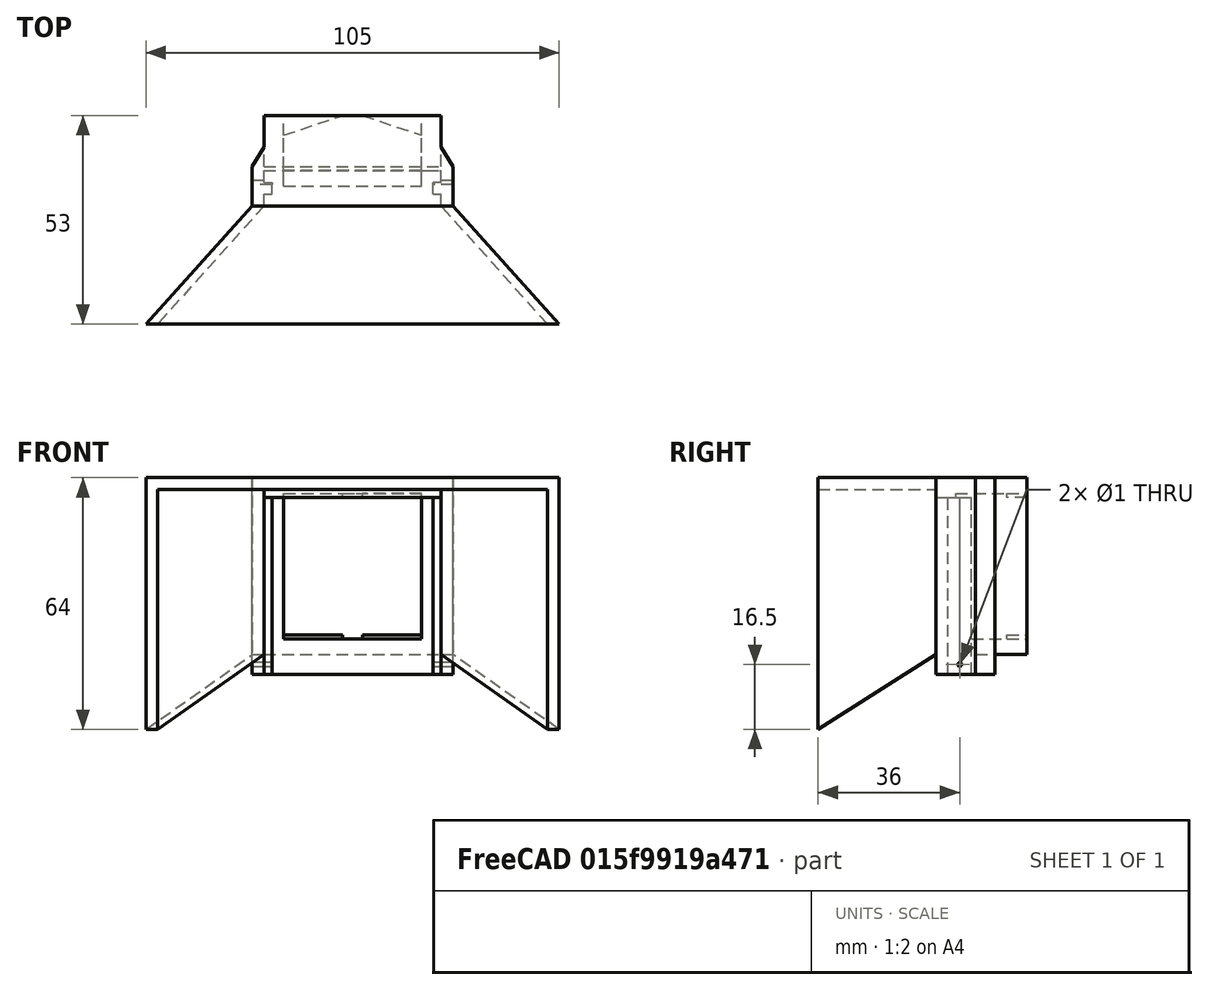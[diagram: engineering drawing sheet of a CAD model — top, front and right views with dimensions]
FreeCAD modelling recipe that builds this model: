
FCSTD DOCUMENT  (FreeCAD 0.20R29603 (Git))
Label: Spritzschutz
License: All rights reserved
LicenseURL: http://en.wikipedia.org/wiki/All_rights_reserved
objects: TechDraw::DrawViewDimension×27, TechDraw::DrawProjGroupItem×15, PartDesign::AdditiveBox×5, PartDesign::SubtractiveBox×4, PartDesign::AdditiveWedge×3, TechDraw::DrawSVGTemplate×2, PartDesign::Body×2, PartDesign::SubtractiveWedge×2, TechDraw::DrawPage×2, TechDraw::DrawProjGroup×2, App::MeasureDistance×1, PartDesign::SubtractiveCylinder×1, TechDraw::DrawViewSection×1
note: 32 computed .brp shape members not serialized (recipe doc carries the construction recipe); baked Part::Feature solids carry a one-line shape summary decoded from their .brp

FEATURE [App::MeasureDistance] Distance  label="Distance: 0,87 mm"
  Distance = 0.87465
  P1 = (0,7.01825,-5)
  P2 = (-0.871183,7.09606,-5)
FEATURE [TechDraw::DrawSVGTemplate] Template
  EditableTexts = Designed_by_Name=B. Schulze; Drawing_number=1; FC-Date=13.09.2023; FC-SC=1:2; FC-SH=8; FC-Title=Eisdosierer; Subtitle=Spritzschutz Teil 1
  Height = 210
  Orientation = 1
  Width = 297
FEATURE [TechDraw::DrawSVGTemplate] Template001
  EditableTexts = Designed_by_Name=B. Schulze; Drawing_number=1; FC-Date=13.09.2023; FC-SC=1:2; FC-SH=9; FC-Title=Eisdosierer; Subtitle=Spritzschutz Teil2
  Height = 210
  Orientation = 1
  Width = 297
FEATURE [PartDesign::Body] Body  label="Teil1"
  Group = -> [Box,Wedge,Box001,Box002,Wedge004,Wedge005,Box005,Box006,Box007,Box008,Box009,Cylinder,Box010]
  Origin = -> Origin
  Tip = -> Box010
FEATURE [PartDesign::AdditiveBox] Box
  AttacherType = Attacher::AttachEngine3D
  Height = 45
  Length = 45
  MapMode = 2
  Support = -> [Body]
  Width = 20
FEATURE [PartDesign::SubtractiveWedge] Wedge
  AttacherType = Attacher::AttachEngine3D
  AttachmentOffset = pos=(5,15,4) rot=(0,0,1;0rad)
  BaseFeature = -> Box
  MapMode = 2
  Placement = pos=(5,15,4) rot=(0,0,1;0rad)
  Support = -> [Body]
  X2max = 20
  X2min = 15
  Xmax = 35
  Xmin = 0
  Ymax = 5
  Ymin = 0
  Z2max = 37
  Z2min = 0
  Zmax = 37
  Zmin = 0
FEATURE [PartDesign::SubtractiveBox] Box001
  AttacherType = Attacher::AttachEngine3D
  AttachmentOffset = pos=(5,0,5) rot=(0,0,1;0rad)
  BaseFeature = -> Wedge
  Height = 35
  Length = 35
  MapMode = 2
  Placement = pos=(5,0,5) rot=(0,0,1;0rad)
  Support = -> [Body]
  Width = 21
FEATURE [PartDesign::SubtractiveBox] Box002
  AttacherType = Attacher::AttachEngine3D
  AttachmentOffset = pos=(5,0,4) rot=(0,0,1;0rad)
  BaseFeature = -> Box001
  Height = 37
  Length = 35
  MapMode = 2
  Placement = pos=(5,0,4) rot=(0,0,1;0rad)
  Support = -> [Body]
  Width = 15
FEATURE [PartDesign::Body] Body002  label="Teil2"
  Group = -> [Wedge002,Wedge003]
  Origin = -> Origin002
  Placement = pos=(0,-3,0) rot=(0,0,1;0rad)
  Tip = -> Wedge003
FEATURE [PartDesign::AdditiveWedge] Wedge002
  AttacherType = Attacher::AttachEngine3D
  AttachmentOffset = pos=(-30,-30,45) rot=(0,1,0;1.5708rad)
  MapMode = 2
  Placement = pos=(-30,-30,45) rot=(0,1,0;1.5708rad)
  Support = -> [Body]
  X2max = 45
  X2min = 0
  Xmax = 64
  Xmin = 0
  Ymax = 30
  Ymin = 0
  Z2max = 78
  Z2min = 27
  Zmax = 105
  Zmin = 0
FEATURE [PartDesign::SubtractiveWedge] Wedge003
  AttacherType = Attacher::AttachEngine3D
  AttachmentOffset = pos=(-27,-30,42) rot=(0,1,0;1.5708rad)
  BaseFeature = -> Wedge002
  MapMode = 2
  Placement = pos=(-27,-30,42) rot=(0,1,0;1.5708rad)
  Support = -> [Body]
  X2max = 45
  X2min = 0
  Xmax = 61
  Xmin = 0
  Ymax = 30
  Ymin = 0
  Z2max = 72
  Z2min = 27
  Zmax = 99
  Zmin = 0
FEATURE [PartDesign::AdditiveWedge] Wedge004
  AttacherType = Attacher::AttachEngine3D
  AttachmentOffset = pos=(-3,7,-5) rot=(0,0,1;0rad)
  BaseFeature = -> Box002
  MapMode = 2
  Placement = pos=(-3,7,-5) rot=(0,0,1;0rad)
  Support = -> [Body]
  X2max = 3
  X2min = 3
  Xmax = 3
  Xmin = 0
  Ymax = 5
  Ymin = 0
  Z2max = 50
  Z2min = 0
  Zmax = 50
  Zmin = 0
FEATURE [PartDesign::AdditiveWedge] Wedge005
  AttacherType = Attacher::AttachEngine3D
  AttachmentOffset = pos=(45,7,-5) rot=(0,0,1;0rad)
  BaseFeature = -> Wedge004
  MapMode = 2
  Placement = pos=(45,7,-5) rot=(0,0,1;0rad)
  Support = -> [Body]
  X2max = 0
  X2min = 0
  Xmax = 3
  Xmin = 0
  Ymax = 5
  Ymin = 0
  Z2max = 50
  Z2min = 0
  Zmax = 50
  Zmin = 0
FEATURE [PartDesign::AdditiveBox] Box005
  AttacherType = Attacher::AttachEngine3D
  AttachmentOffset = pos=(0,0,-5) rot=(0,0,1;0rad)
  BaseFeature = -> Wedge005
  Height = 5
  Length = 45
  MapMode = 2
  Placement = pos=(0,0,-5) rot=(0,0,1;0rad)
  Support = -> [Body]
  Width = 7
FEATURE [PartDesign::SubtractiveBox] Box006
  AttacherType = Attacher::AttachEngine3D
  AttachmentOffset = pos=(0,3,-5) rot=(0,0,1;0rad)
  BaseFeature = -> Box005
  Height = 45
  Length = 45
  MapMode = 2
  Placement = pos=(0,3,-5) rot=(0,0,1;0rad)
  Support = -> [Body]
  Width = 3
FEATURE [PartDesign::AdditiveBox] Box007
  AttacherType = Attacher::AttachEngine3D
  AttachmentOffset = pos=(-3,-3,-5) rot=(0,0,1;0rad)
  BaseFeature = -> Box006
  Height = 50
  Length = 3
  MapMode = 2
  Placement = pos=(-3,-3,-5) rot=(0,0,1;0rad)
  Support = -> [Body]
  Width = 10
FEATURE [PartDesign::AdditiveBox] Box008
  AttacherType = Attacher::AttachEngine3D
  AttachmentOffset = pos=(45,-3,-5) rot=(0,0,1;0rad)
  BaseFeature = -> Box007
  Height = 50
  Length = 3
  MapMode = 2
  Placement = pos=(45,-3,-5) rot=(0,0,1;0rad)
  Support = -> [Body]
  Width = 10
FEATURE [PartDesign::SubtractiveBox] Box009
  AttacherType = Attacher::AttachEngine3D
  AttachmentOffset = pos=(2,0,-5) rot=(0,0,1;0rad)
  BaseFeature = -> Box008
  Height = 45
  Length = 41
  MapMode = 2
  Placement = pos=(2,0,-5) rot=(0,0,1;0rad)
  Support = -> [Body]
  Width = 3
FEATURE [PartDesign::SubtractiveCylinder] Cylinder
  Angle = 360
  AttacherType = Attacher::AttachEngine3D
  AttachmentOffset = pos=(-3,3,-2.5) rot=(0,1,0;1.5708rad)
  BaseFeature = -> Box009
  FirstAngle = 0
  Height = 51
  MapMode = 2
  Placement = pos=(-3,3,-2.5) rot=(0,1,0;1.5708rad)
  Radius = 0.5
  SecondAngle = 0
  Support = -> [Body]
FEATURE [PartDesign::AdditiveBox] Box010
  AttacherType = Attacher::AttachEngine3D
  AttachmentOffset = pos=(0,-3,40) rot=(0,0,1;0rad)
  BaseFeature = -> Cylinder
  Height = 5
  Length = 45
  MapMode = 2
  Placement = pos=(0,-3,40) rot=(0,0,1;0rad)
  Support = -> [Body]
  Width = 5
FEATURE [TechDraw::DrawPage] Page
  KeepUpdated = true
  NextBalloonIndex = 1
  ProjectionType = 0
  Template = -> Template
  Views = -> [ProjGroup,Dimension,Dimension001,Dimension002,Dimension003,Dimension004,Dimension005,Dimension006,Dimension007,SectionView,Dimension008,Dimension009,Dimension010,Dimension011,Dimension012,Dimension013,Dimension014]
FEATURE [TechDraw::DrawProjGroup] ProjGroup
  Anchor = -> ProjItem
  AutoDistribute = false
  LockPosition = false
  ProjectionType = 0
  Rotation = 0
  Scale = 0.5
  ScaleType = 2
  Source = -> [Body]
  Views = -> [ProjItem,ProjItem001,ProjItem002,ProjItem003,ProjItem004,ProjItem005,ProjItem007,ProjItem008]
  X = 102.37
  Y = 112.924
  spacingX = 15
  spacingY = 15
FEATURE [TechDraw::DrawProjGroupItem] ProjItem  label="Front"
  CoarseView = false
  Direction = (0,0,-1)
  Focus = 100
  HardHidden = false
  IsoCount = 0
  IsoHidden = false
  IsoVisible = false
  LockPosition = true
  Perspective = false
  Rotation = 0
  RotationVector = (1,0,0)
  Scale = 0.5
  ScaleType = 2
  SeamHidden = false
  SeamVisible = true
  SmoothHidden = false
  SmoothVisible = true
  Source = -> [Body]
  Type = 0
  X = 0
  XDirection = (1,0,0)
  Y = 0
FEATURE [TechDraw::DrawProjGroupItem] ProjItem001  label="FrontBottomRight"
  CoarseView = false
  Direction = (0.57735,0.57735,-0.57735)
  Focus = 100
  HardHidden = false
  IsoCount = 0
  IsoHidden = false
  IsoVisible = false
  LockPosition = false
  Perspective = false
  Rotation = 0
  RotationVector = (1,0,0)
  Scale = 0.5
  ScaleType = 2
  SeamHidden = false
  SeamVisible = true
  SmoothHidden = false
  SmoothVisible = true
  Source = -> [Body]
  Type = 9
  X = -50.7089
  XDirection = (0.707107,0,0.707107)
  Y = 50.7089
FEATURE [TechDraw::DrawProjGroupItem] ProjItem002  label="Bottom"
  CoarseView = false
  Direction = (0,1,0)
  Focus = 100
  HardHidden = false
  IsoCount = 0
  IsoHidden = false
  IsoVisible = false
  LockPosition = false
  Perspective = false
  Rotation = 0
  RotationVector = (1,0,0)
  Scale = 0.5
  ScaleType = 2
  SeamHidden = false
  SeamVisible = true
  SmoothHidden = false
  SmoothVisible = true
  Source = -> [Body]
  Type = 5
  X = 0
  XDirection = (1,0,0)
  Y = 50.7089
FEATURE [TechDraw::DrawProjGroupItem] ProjItem003  label="FrontBottomLeft"
  CoarseView = false
  Direction = (-0.57735,0.57735,-0.57735)
  Focus = 100
  HardHidden = false
  IsoCount = 0
  IsoHidden = false
  IsoVisible = false
  LockPosition = false
  Perspective = false
  Rotation = 0
  RotationVector = (1,0,0)
  Scale = 0.5
  ScaleType = 2
  SeamHidden = false
  SeamVisible = true
  SmoothHidden = false
  SmoothVisible = true
  Source = -> [Body]
  Type = 8
  X = 127.121
  XDirection = (0.707107,0,-0.707107)
  Y = 53.4258
FEATURE [TechDraw::DrawProjGroupItem] ProjItem004  label="Left"
  CoarseView = false
  Direction = (-1,0,-1e-16)
  Focus = 100
  HardHidden = false
  IsoCount = 0
  IsoHidden = false
  IsoVisible = false
  LockPosition = false
  Perspective = false
  Rotation = 0
  RotationVector = (1,0,0)
  Scale = 0.5
  ScaleType = 2
  SeamHidden = false
  SeamVisible = true
  SmoothHidden = false
  SmoothVisible = true
  Source = -> [Body]
  Type = 1
  X = 50.7089
  XDirection = (1e-16,0,-1)
  Y = 0
FEATURE [TechDraw::DrawProjGroupItem] ProjItem005  label="Rear"
  CoarseView = false
  Direction = (0,0,1)
  Focus = 100
  HardHidden = false
  IsoCount = 0
  IsoHidden = false
  IsoVisible = false
  LockPosition = false
  Perspective = false
  Rotation = 0
  RotationVector = (1,0,0)
  Scale = 0.5
  ScaleType = 2
  SeamHidden = false
  SeamVisible = true
  SmoothHidden = false
  SmoothVisible = true
  Source = -> [Body]
  Type = 3
  X = 101.418
  XDirection = (-1,0,0)
  Y = 0
FEATURE [TechDraw::DrawProjGroupItem] ProjItem007  label="Top"
  CoarseView = false
  Direction = (0,-1,0)
  Focus = 100
  HardHidden = false
  IsoCount = 0
  IsoHidden = false
  IsoVisible = false
  LockPosition = false
  Perspective = false
  Rotation = 0
  RotationVector = (1,0,0)
  Scale = 0.5
  ScaleType = 2
  SeamHidden = false
  SeamVisible = true
  SmoothHidden = false
  SmoothVisible = true
  Source = -> [Body]
  Type = 4
  X = 0
  XDirection = (1,0,0)
  Y = -50.7089
FEATURE [TechDraw::DrawProjGroupItem] ProjItem008  label="FrontTopRight"
  CoarseView = false
  Direction = (0.57735,-0.57735,-0.57735)
  Focus = 100
  HardHidden = false
  IsoCount = 0
  IsoHidden = false
  IsoVisible = false
  LockPosition = false
  Perspective = false
  Rotation = 0
  RotationVector = (1,0,0)
  Scale = 0.5
  ScaleType = 2
  SeamHidden = false
  SeamVisible = true
  SmoothHidden = false
  SmoothVisible = true
  Source = -> [Body]
  Type = 7
  X = -60.5262
  XDirection = (0.707107,0,0.707107)
  Y = -23.5822
FEATURE [TechDraw::DrawViewDimension] Dimension
  AngleOverride = false
  Arbitrary = false
  ArbitraryTolerances = false
  EqualTolerance = true
  ExtensionAngle = 0
  FormatSpec = %.2w
  FormatSpecOverTolerance = %+.2w
  FormatSpecUnderTolerance = %+.2w
  Inverted = false
  LineAngle = 0
  LockPosition = false
  MeasureType = 1
  OverTolerance = 0
  References2D = -> [ProjItem004]
  Rotation = 0
  ScaleType = 0
  TheoreticalExact = false
  Type = 1
  UnderTolerance = 0
  X = -1.15522
  Y = -6.8516
FEATURE [TechDraw::DrawViewDimension] Dimension001
  AngleOverride = false
  Arbitrary = false
  ArbitraryTolerances = false
  EqualTolerance = true
  ExtensionAngle = 0
  FormatSpec = %.2w
  FormatSpecOverTolerance = %+.2w
  FormatSpecUnderTolerance = %+.2w
  Inverted = false
  LineAngle = 0
  LockPosition = false
  MeasureType = 1
  OverTolerance = 0
  References2D = -> [ProjItem004]
  Rotation = 0
  ScaleType = 0
  TheoreticalExact = false
  Type = 1
  UnderTolerance = 0
  X = 0.758231
  Y = 19.4339
FEATURE [TechDraw::DrawViewDimension] Dimension002
  AngleOverride = false
  Arbitrary = false
  ArbitraryTolerances = false
  EqualTolerance = true
  ExtensionAngle = 0
  FormatSpec = %.2w
  FormatSpecOverTolerance = %+.2w
  FormatSpecUnderTolerance = %+.2w
  Inverted = false
  LineAngle = 0
  LockPosition = false
  MeasureType = 1
  OverTolerance = 0
  References2D = -> [ProjItem005]
  Rotation = 0
  ScaleType = 0
  TheoreticalExact = false
  Type = 1
  UnderTolerance = 0
  X = 0
  Y = -13.5604
FEATURE [TechDraw::DrawViewDimension] Dimension003
  AngleOverride = false
  Arbitrary = false
  ArbitraryTolerances = false
  EqualTolerance = true
  ExtensionAngle = 0
  FormatSpec = %.2w
  FormatSpecOverTolerance = %+.2w
  FormatSpecUnderTolerance = %+.2w
  Inverted = false
  LineAngle = 0
  LockPosition = false
  MeasureType = 1
  OverTolerance = 0
  References2D = -> [ProjItem005]
  Rotation = 0
  ScaleType = 0
  TheoreticalExact = false
  Type = 2
  UnderTolerance = 0
  X = -24.9622
  Y = -0.098174
FEATURE [TechDraw::DrawViewDimension] Dimension004
  AngleOverride = false
  Arbitrary = false
  ArbitraryTolerances = false
  EqualTolerance = true
  ExtensionAngle = 0
  FormatSpec = %.2w
  FormatSpecOverTolerance = %+.2w
  FormatSpecUnderTolerance = %+.2w
  Inverted = false
  LineAngle = 0
  LockPosition = false
  MeasureType = 1
  OverTolerance = 0
  References2D = -> [ProjItem005]
  Rotation = 0
  ScaleType = 0
  TheoreticalExact = false
  Type = 2
  UnderTolerance = 0
  X = -18.8757
  Y = 6.06147
FEATURE [TechDraw::DrawViewDimension] Dimension005
  AngleOverride = false
  Arbitrary = false
  ArbitraryTolerances = false
  EqualTolerance = true
  ExtensionAngle = 0
  FormatSpec = %.2w
  FormatSpecOverTolerance = %+.2w
  FormatSpecUnderTolerance = %+.2w
  Inverted = false
  LineAngle = 0
  LockPosition = false
  MeasureType = 1
  OverTolerance = 0
  References2D = -> [ProjItem005]
  Rotation = 0
  ScaleType = 0
  TheoreticalExact = false
  Type = 2
  UnderTolerance = 0
  X = 27.4294
  Y = -1.02823
FEATURE [TechDraw::DrawViewDimension] Dimension006
  AngleOverride = false
  Arbitrary = false
  ArbitraryTolerances = false
  EqualTolerance = true
  ExtensionAngle = 0
  FormatSpec = %.2w
  FormatSpecOverTolerance = %+.2w
  FormatSpecUnderTolerance = %+.2w
  Inverted = false
  LineAngle = 0
  LockPosition = false
  MeasureType = 1
  OverTolerance = 0
  References2D = -> [ProjItem005]
  Rotation = 0
  ScaleType = 0
  TheoreticalExact = false
  Type = 0
  UnderTolerance = 0
  X = 16.153
  Y = -6.82513
FEATURE [TechDraw::DrawViewDimension] Dimension007
  AngleOverride = false
  Arbitrary = false
  ArbitraryTolerances = false
  EqualTolerance = true
  ExtensionAngle = 0
  FormatSpec = %.2w
  FormatSpecOverTolerance = %+.2w
  FormatSpecUnderTolerance = %+.2w
  Inverted = false
  LineAngle = 0
  LockPosition = false
  MeasureType = 1
  OverTolerance = 0
  References2D = -> [ProjItem005]
  Rotation = 0
  ScaleType = 0
  TheoreticalExact = false
  Type = 1
  UnderTolerance = 0
  X = 12.2194
  Y = 12.5831
FEATURE [TechDraw::DrawViewSection] SectionView  label="Section  - "
  BaseView = -> ProjItem002
  CoarseView = false
  CutSurfaceDisplay = 2
  Direction = (0,0,1)
  FileGeomPattern = <path> 0.20/data/Mod/TechDraw/PAT/FCPAT.pat
  FileHatchPattern = <path> 0.20/data/Mod/TechDraw/Patterns/simple.svg
  Focus = 100
  FuseBeforeCut = false
  HardHidden = false
  HatchScale = 1
  IsoCount = 0
  IsoHidden = false
  IsoVisible = false
  LockPosition = false
  NameGeomPattern = Diamant
  Perspective = false
  Rotation = 0
  ScaleType = 2
  SeamHidden = false
  SeamVisible = true
  SectionDirection = 2
  SectionNormal = (0,0,1)
  SectionOrigin = (22.5,7.5,39)
  SmoothHidden = false
  SmoothVisible = true
  Source = -> [Body]
  X = 158.364
  XDirection = (1,0,0)
  Y = 167.54
FEATURE [TechDraw::DrawViewDimension] Dimension008
  AngleOverride = false
  Arbitrary = false
  ArbitraryTolerances = false
  EqualTolerance = true
  ExtensionAngle = 0
  FormatSpec = %.2w
  FormatSpecOverTolerance = %+.2w
  FormatSpecUnderTolerance = %+.2w
  Inverted = false
  LineAngle = 0
  LockPosition = false
  MeasureType = 1
  OverTolerance = 0
  References2D = -> [SectionView]
  Rotation = 0
  ScaleType = 0
  TheoreticalExact = false
  Type = 1
  UnderTolerance = 0
  X = 0.615924
  Y = -24.9563
FEATURE [TechDraw::DrawViewDimension] Dimension009
  AngleOverride = false
  Arbitrary = false
  ArbitraryTolerances = false
  EqualTolerance = true
  ExtensionAngle = 0
  FormatSpec = %.2w
  FormatSpecOverTolerance = %+.2w
  FormatSpecUnderTolerance = %+.2w
  Inverted = false
  LineAngle = 0
  LockPosition = false
  MeasureType = 1
  OverTolerance = 0
  References2D = -> [SectionView]
  Rotation = 0
  ScaleType = 0
  TheoreticalExact = false
  Type = 0
  UnderTolerance = 0
  X = -7.24262
  Y = 11.3607
FEATURE [TechDraw::DrawViewDimension] Dimension010
  AngleOverride = false
  Arbitrary = false
  ArbitraryTolerances = false
  EqualTolerance = true
  ExtensionAngle = 0
  FormatSpec = %.2w
  FormatSpecOverTolerance = %+.2w
  FormatSpecUnderTolerance = %+.2w
  Inverted = false
  LineAngle = 0
  LockPosition = false
  MeasureType = 1
  OverTolerance = 0
  References2D = -> [SectionView]
  Rotation = 0
  ScaleType = 0
  TheoreticalExact = false
  Type = 1
  UnderTolerance = 0
  X = -0.014053
  Y = 5.45686
FEATURE [TechDraw::DrawViewDimension] Dimension011
  AngleOverride = false
  Arbitrary = false
  ArbitraryTolerances = false
  EqualTolerance = true
  ExtensionAngle = 0
  FormatSpec = %.2w
  FormatSpecOverTolerance = %+.2w
  FormatSpecUnderTolerance = %+.2w
  Inverted = false
  LineAngle = 0
  LockPosition = false
  MeasureType = 1
  OverTolerance = 0
  References2D = -> [SectionView]
  Rotation = 0
  ScaleType = 0
  TheoreticalExact = false
  Type = 1
  UnderTolerance = 0
  X = -20.6811
  Y = -19.7573
FEATURE [TechDraw::DrawViewDimension] Dimension012
  AngleOverride = false
  Arbitrary = false
  ArbitraryTolerances = false
  EqualTolerance = true
  ExtensionAngle = 0
  FormatSpec = %.2w
  FormatSpecOverTolerance = %+.2w
  FormatSpecUnderTolerance = %+.2w
  Inverted = false
  LineAngle = 0
  LockPosition = false
  MeasureType = 1
  OverTolerance = 0
  References2D = -> [SectionView]
  Rotation = 0
  ScaleType = 0
  TheoreticalExact = false
  Type = 2
  UnderTolerance = 0
  X = -17.552
  Y = -4.82756
FEATURE [TechDraw::DrawViewDimension] Dimension013
  AngleOverride = false
  Arbitrary = false
  ArbitraryTolerances = false
  EqualTolerance = true
  ExtensionAngle = 0
  FormatSpec = %.2w
  FormatSpecOverTolerance = %+.2w
  FormatSpecUnderTolerance = %+.2w
  Inverted = false
  LineAngle = 0
  LockPosition = false
  MeasureType = 1
  OverTolerance = 0
  References2D = -> [SectionView]
  Rotation = 0
  ScaleType = 0
  TheoreticalExact = false
  Type = 2
  UnderTolerance = 0
  X = 5.63088
  Y = -1.99133
FEATURE [TechDraw::DrawViewDimension] Dimension014
  AngleOverride = false
  Arbitrary = false
  ArbitraryTolerances = false
  EqualTolerance = true
  ExtensionAngle = 0
  FormatSpec = %.2w
  FormatSpecOverTolerance = %+.2w
  FormatSpecUnderTolerance = %+.2w
  Inverted = false
  LineAngle = 0
  LockPosition = false
  MeasureType = 1
  OverTolerance = 0
  References2D = -> [SectionView]
  Rotation = 0
  ScaleType = 0
  TheoreticalExact = false
  Type = 2
  UnderTolerance = 0
  X = 12.6733
  Y = -7.99133
FEATURE [TechDraw::DrawPage] Page001
  KeepUpdated = true
  NextBalloonIndex = 1
  ProjectionType = 0
  Template = -> Template001
  Views = -> [ProjGroup001,Dimension015,Dimension016,Dimension017,Dimension018,Dimension019,Dimension020,Dimension021,Dimension022,Dimension023,Dimension024,Dimension025,Dimension026]
FEATURE [TechDraw::DrawProjGroup] ProjGroup001
  Anchor = -> ProjItem009
  AutoDistribute = false
  LockPosition = false
  ProjectionType = 0
  Rotation = 0
  Scale = 0.5
  ScaleType = 2
  Source = -> [Body002]
  Views = -> [ProjItem009,ProjItem010,ProjItem011,ProjItem013,ProjItem014,ProjItem015,ProjItem018]
  X = 130.886
  Y = 113.932
  spacingX = 15
  spacingY = 15
FEATURE [TechDraw::DrawProjGroupItem] ProjItem009  label="Front001"
  CoarseView = false
  Direction = (-2e-16,0,1)
  Focus = 100
  HardHidden = false
  IsoCount = 0
  IsoHidden = false
  IsoVisible = false
  LockPosition = true
  Perspective = false
  Rotation = 0
  RotationVector = (1,0,0)
  Scale = 0.5
  ScaleType = 2
  SeamHidden = false
  SeamVisible = true
  SmoothHidden = false
  SmoothVisible = true
  Source = -> [Body002]
  Type = 0
  X = 0
  XDirection = (-1,0,-2e-16)
  Y = 0
FEATURE [TechDraw::DrawProjGroupItem] ProjItem010  label="Left001"
  CoarseView = false
  Direction = (1,0,3e-16)
  Focus = 100
  HardHidden = false
  IsoCount = 0
  IsoHidden = false
  IsoVisible = false
  LockPosition = false
  Perspective = false
  Rotation = 0
  RotationVector = (1,0,0)
  ScaleType = 2
  SeamHidden = false
  SeamVisible = true
  SmoothHidden = false
  SmoothVisible = true
  Source = -> [Body002]
  Type = 1
  X = 67.5
  XDirection = (-3e-16,0,1)
  Y = 0
FEATURE [TechDraw::DrawProjGroupItem] ProjItem011  label="Right"
  CoarseView = false
  Direction = (-1,0,-1e-16)
  Focus = 100
  HardHidden = false
  IsoCount = 0
  IsoHidden = false
  IsoVisible = false
  LockPosition = false
  Perspective = false
  Rotation = 0
  RotationVector = (1,0,0)
  ScaleType = 2
  SeamHidden = false
  SeamVisible = true
  SmoothHidden = false
  SmoothVisible = true
  Source = -> [Body002]
  Type = 2
  X = -67.5
  XDirection = (1e-16,0,-1)
  Y = 0
FEATURE [TechDraw::DrawProjGroupItem] ProjItem013  label="Bottom001"
  CoarseView = false
  Direction = (0,1,0)
  Focus = 100
  HardHidden = false
  IsoCount = 0
  IsoHidden = false
  IsoVisible = false
  LockPosition = false
  Perspective = false
  Rotation = 0
  RotationVector = (1,0,0)
  ScaleType = 2
  SeamHidden = false
  SeamVisible = true
  SmoothHidden = false
  SmoothVisible = true
  Source = -> [Body002]
  Type = 5
  X = 0
  XDirection = (-1,0,-2e-16)
  Y = 55.5265
FEATURE [TechDraw::DrawProjGroupItem] ProjItem014  label="Top001"
  CoarseView = false
  Direction = (0,-1,0)
  Focus = 100
  HardHidden = false
  IsoCount = 0
  IsoHidden = false
  IsoVisible = false
  LockPosition = false
  Perspective = false
  Rotation = 0
  RotationVector = (1,0,0)
  ScaleType = 2
  SeamHidden = false
  SeamVisible = true
  SmoothHidden = false
  SmoothVisible = true
  Source = -> [Body002]
  Type = 4
  X = 0
  XDirection = (-1,0,-2e-16)
  Y = -41.4255
FEATURE [TechDraw::DrawProjGroupItem] ProjItem015  label="FrontBottomLeft001"
  CoarseView = false
  Direction = (0.57735,0.57735,0.57735)
  Focus = 100
  HardHidden = false
  IsoCount = 0
  IsoHidden = false
  IsoVisible = false
  LockPosition = false
  Perspective = false
  Rotation = 0
  RotationVector = (1,0,0)
  ScaleType = 2
  SeamHidden = false
  SeamVisible = true
  SmoothHidden = false
  SmoothVisible = true
  Source = -> [Body002]
  Type = 8
  X = 74.7505
  XDirection = (-0.707107,0,0.707107)
  Y = 55.4053
FEATURE [TechDraw::DrawProjGroupItem] ProjItem018  label="FrontBottomRight001"
  CoarseView = false
  Direction = (-0.57735,0.57735,0.57735)
  Focus = 100
  HardHidden = false
  IsoCount = 0
  IsoHidden = false
  IsoVisible = false
  LockPosition = false
  Perspective = false
  Rotation = 0
  RotationVector = (1,0,0)
  ScaleType = 2
  SeamHidden = false
  SeamVisible = true
  SmoothHidden = false
  SmoothVisible = true
  Source = -> [Body002]
  Type = 9
  X = -83.3071
  XDirection = (-0.707107,0,-0.707107)
  Y = 47.4446
FEATURE [TechDraw::DrawViewDimension] Dimension015
  AngleOverride = false
  Arbitrary = false
  ArbitraryTolerances = false
  EqualTolerance = true
  ExtensionAngle = 0
  FormatSpec = %.2w
  FormatSpecOverTolerance = %+.2w
  FormatSpecUnderTolerance = %+.2w
  Inverted = false
  LineAngle = 0
  LockPosition = false
  MeasureType = 1
  OverTolerance = 0
  References2D = -> [ProjItem013]
  Rotation = 0
  ScaleType = 0
  TheoreticalExact = false
  Type = 1
  UnderTolerance = 0
  X = 0
  Y = 25.811
FEATURE [TechDraw::DrawViewDimension] Dimension016
  AngleOverride = false
  Arbitrary = false
  ArbitraryTolerances = false
  EqualTolerance = true
  ExtensionAngle = 0
  FormatSpec = %.2w
  FormatSpecOverTolerance = %+.2w
  FormatSpecUnderTolerance = %+.2w
  Inverted = false
  LineAngle = 0
  LockPosition = false
  MeasureType = 1
  OverTolerance = 0
  References2D = -> [ProjItem013]
  Rotation = 0
  ScaleType = 0
  TheoreticalExact = false
  Type = 1
  UnderTolerance = 0
  X = 0.47168
  Y = -1.39553
FEATURE [TechDraw::DrawViewDimension] Dimension017
  AngleOverride = false
  Arbitrary = false
  ArbitraryTolerances = false
  EqualTolerance = true
  ExtensionAngle = 0
  FormatSpec = %.2w
  FormatSpecOverTolerance = %+.2w
  FormatSpecUnderTolerance = %+.2w
  Inverted = false
  LineAngle = 0
  LockPosition = false
  MeasureType = 1
  OverTolerance = 0
  References2D = -> [ProjItem013]
  Rotation = 0
  ScaleType = 0
  TheoreticalExact = false
  Type = 2
  UnderTolerance = 0
  X = -38.2207
  Y = 10.5518
FEATURE [TechDraw::DrawViewDimension] Dimension018
  AngleOverride = false
  Arbitrary = false
  ArbitraryTolerances = false
  EqualTolerance = true
  ExtensionAngle = 0
  FormatSpec = %.2w
  FormatSpecOverTolerance = %+.2w
  FormatSpecUnderTolerance = %+.2w
  Inverted = false
  LineAngle = 0
  LockPosition = false
  MeasureType = 1
  OverTolerance = 0
  References2D = -> [ProjItem013]
  Rotation = 0
  ScaleType = 0
  TheoreticalExact = false
  Type = 2
  UnderTolerance = 0
  X = 14.7644
  Y = 3.62945
FEATURE [TechDraw::DrawViewDimension] Dimension019
  AngleOverride = false
  Arbitrary = false
  ArbitraryTolerances = false
  EqualTolerance = true
  ExtensionAngle = 0
  FormatSpec = %.2w
  FormatSpecOverTolerance = %+.2w
  FormatSpecUnderTolerance = %+.2w
  Inverted = false
  LineAngle = 0
  LockPosition = false
  MeasureType = 1
  OverTolerance = 0
  References2D = -> [ProjItem013]
  Rotation = 0
  ScaleType = 0
  TheoreticalExact = false
  Type = 1
  UnderTolerance = 0
  X = -24.9809
  Y = -19.5219
FEATURE [TechDraw::DrawViewDimension] Dimension020
  AngleOverride = false
  Arbitrary = false
  ArbitraryTolerances = false
  EqualTolerance = true
  ExtensionAngle = 0
  FormatSpec = %.2w
  FormatSpecOverTolerance = %+.2w
  FormatSpecUnderTolerance = %+.2w
  Inverted = false
  LineAngle = 0
  LockPosition = false
  MeasureType = 1
  OverTolerance = 0
  References2D = -> [ProjItem013]
  Rotation = 0
  ScaleType = 0
  TheoreticalExact = false
  Type = 0
  UnderTolerance = 0
  X = 17.3197
  Y = -13.2145
FEATURE [TechDraw::DrawViewDimension] Dimension021
  AngleOverride = false
  Arbitrary = false
  ArbitraryTolerances = false
  EqualTolerance = true
  ExtensionAngle = 0
  FormatSpec = %.2w
  FormatSpecOverTolerance = %+.2w
  FormatSpecUnderTolerance = %+.2w
  Inverted = false
  LineAngle = 0
  LockPosition = false
  MeasureType = 1
  OverTolerance = 0
  References2D = -> [ProjItem013]
  Rotation = 0
  ScaleType = 0
  TheoreticalExact = false
  Type = 0
  UnderTolerance = 0
  X = -15.9235
  Y = -12.5915
FEATURE [TechDraw::DrawViewDimension] Dimension022
  AngleOverride = false
  Arbitrary = false
  ArbitraryTolerances = false
  EqualTolerance = true
  ExtensionAngle = 0
  FormatSpec = %.2w
  FormatSpecOverTolerance = %+.2w
  FormatSpecUnderTolerance = %+.2w
  Inverted = false
  LineAngle = 0
  LockPosition = false
  MeasureType = 1
  OverTolerance = 0
  References2D = -> [ProjItem013]
  Rotation = 0
  ScaleType = 0
  TheoreticalExact = false
  Type = 2
  UnderTolerance = 0
  X = 32.9376
  Y = 2.09056
FEATURE [TechDraw::DrawViewDimension] Dimension023
  AngleOverride = false
  Arbitrary = false
  ArbitraryTolerances = false
  EqualTolerance = true
  ExtensionAngle = 0
  FormatSpec = %.2w
  FormatSpecOverTolerance = %+.2w
  FormatSpecUnderTolerance = %+.2w
  Inverted = false
  LineAngle = 0
  LockPosition = false
  MeasureType = 1
  OverTolerance = 0
  References2D = -> [ProjItem009]
  Rotation = 0
  ScaleType = 0
  TheoreticalExact = false
  Type = 1
  UnderTolerance = 0
  X = -5.3413
  Y = -8.84356
FEATURE [TechDraw::DrawViewDimension] Dimension024
  AngleOverride = false
  Arbitrary = false
  ArbitraryTolerances = false
  EqualTolerance = true
  ExtensionAngle = 0
  FormatSpec = %.2w
  FormatSpecOverTolerance = %+.2w
  FormatSpecUnderTolerance = %+.2w
  Inverted = false
  LineAngle = 0
  LockPosition = false
  MeasureType = 1
  OverTolerance = 0
  References2D = -> [ProjItem009]
  Rotation = 0
  ScaleType = 0
  TheoreticalExact = false
  Type = 2
  UnderTolerance = 0
  X = -5.50605
  Y = 1.63883
FEATURE [TechDraw::DrawViewDimension] Dimension025
  AngleOverride = false
  Arbitrary = false
  ArbitraryTolerances = false
  EqualTolerance = true
  ExtensionAngle = 0
  FormatSpec = %.2w
  FormatSpecOverTolerance = %+.2w
  FormatSpecUnderTolerance = %+.2w
  Inverted = false
  LineAngle = 0
  LockPosition = false
  MeasureType = 1
  OverTolerance = 0
  References2D = -> [ProjItem009]
  Rotation = 0
  ScaleType = 0
  TheoreticalExact = false
  Type = 0
  UnderTolerance = 0
  X = -25.5282
  Y = -2.02112
FEATURE [TechDraw::DrawViewDimension] Dimension026
  AngleOverride = false
  Arbitrary = false
  ArbitraryTolerances = false
  EqualTolerance = true
  ExtensionAngle = 0
  FormatSpec = %.2w
  FormatSpecOverTolerance = %+.2w
  FormatSpecUnderTolerance = %+.2w
  Inverted = false
  LineAngle = 0
  LockPosition = false
  MeasureType = 1
  OverTolerance = 0
  References2D = -> [ProjItem009]
  Rotation = 0
  ScaleType = 0
  TheoreticalExact = false
  Type = 1
  UnderTolerance = 0
  X = 0.215292
  Y = 16.8893
note: 2 file-system paths scrubbed to <path> (originals preserved in the JSON sidecar)
